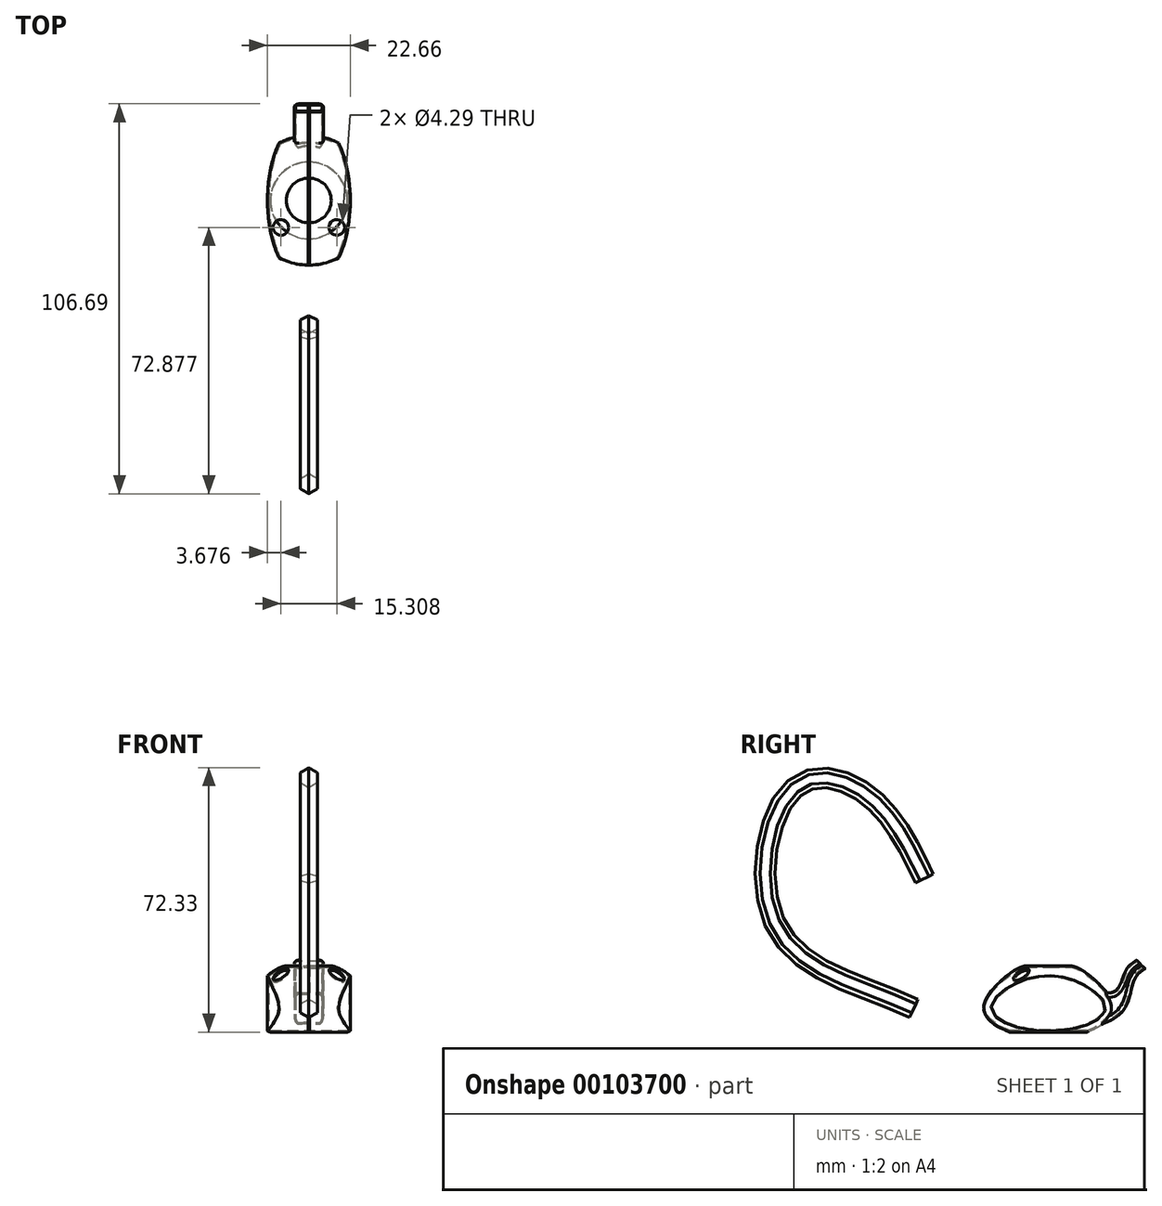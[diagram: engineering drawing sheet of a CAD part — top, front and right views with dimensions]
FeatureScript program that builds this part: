
annotation { "Feature Type Name" : "Feature", "Feature Type Description" : "" }
export const myFeature = defineFeature(function(context is Context, id is Id, definition is map)
    precondition{}
    {
        {
            assignVariable(context, id + "F0", {"name" : "shell_thickness", "anyValue" : 0.4});
        }
        {
            var Q0;
            Q0=qCreatedBy(makeId("Front.planeOp"),FACE);
            var sketch = newSketch(context, id + "F1", { "sketchPlane" : qUnion([Q0])});
            skLineSegment(sketch, "E0", {"start": v(0, 0) * mm, "end": v(-10.55, 0) * mm});
            skLineSegment(sketch, "E1", {"start": v(0, 0) * mm, "end": v(0, 20.96) * mm});
            skFitSpline(sketch, "E2", {"points": [v(-10.55, 0) * mm, v(-17.73, 6.7) * mm, v(-10.87, 15.78) * mm, v(-6.12, 18.17) * mm], "startDerivative": vector(-32.13, 11.4) * mm, "endDerivative": vector(19.24, 3.91) * mm});
            skLineSegment(sketch, "E3", {"start": v(-6.12, 18.17) * mm, "end": v(0, 18.17) * mm});
            skSolve(sketch);
        }
        {
            var Q0;
            Q0=makeQuery(id+"F1.imprint","IMPRINT",FACE,{"disambiguationData":[TD([[makeQuery(id+"F1.imprint","IMPRINT",EDGE,{"derivedFrom":sQuery(id+"F1.wireOp",EDGE,"E0")}),-1.0]])]});
            var Q1;
            Q1=sQuery(id+"F1.wireOp",EDGE,"E1");
            revolve(context, id + "F2", {"entities" : qUnion([Q0]), "axis" : qUnion([Q1]), "revolveType" : RevolveType.FULL});
        }
        {
            var Q0;
            Q0=qCreatedBy(makeId("Top.planeOp"),FACE);
            var sketch = newSketch(context, id + "F3", { "sketchPlane" : qUnion([Q0])});
            skEllipse(sketch, "E4", {"center": v(0, 0) * mm, "majorRadius": 22.7 * mm, "minorRadius": 11.33 * mm, "majorAxis": v(0, 1)});
            skSolve(sketch);
        }
        {
            var Q0;
            Q0=makeQuery(id+"F3.imprint","IMPRINT",FACE,{"disambiguationData":[TD([[makeQuery(id+"F3.imprint","IMPRINT",EDGE,{"derivedFrom":sQuery(id+"F3.wireOp",EDGE,"E4")}),1.0]])]});
            extrude(context, id + "F4", {"entities" : qUnion([Q0]), "operationType" : NewBodyOperationType.INTERSECT, "oppositeDirection" : true, "depth" : 25.4 * mm, "hasSecondDirection" : true, "secondDirectionOppositeDirection" : false, "secondDirectionDepth" : 25.4 * mm});
        }
        {
            var Q0;
            Q0=qCreatedBy(makeId("Right.planeOp"),FACE);
            var sketch = newSketch(context, id + "F5", { "sketchPlane" : qUnion([Q0])});
            skFitSpline(sketch, "E5", {"points": [v(13.8, 1.95) * mm, v(21.7, 8.15) * mm, v(23.96, 15.15) * mm, v(26.43, 17.37) * mm], "startDerivative": vector(35.23, 10.07) * mm, "endDerivative": vector(9.39, 6.72) * mm});
            skFitSpline(sketch, "E6", {"points": [v(14.11, 11.15) * mm, v(18.73, 11.69) * mm, v(21.6, 17.51) * mm, v(24.16, 19.7) * mm], "startDerivative": vector(18.22, -5.52) * mm, "endDerivative": vector(8.5, 6.7) * mm});
            skLineSegment(sketch, "E7", {"start": v(13.8, 1.95) * mm, "end": v(14.11, 11.15) * mm});
            skLineSegment(sketch, "E8", {"start": v(26.43, 17.37) * mm, "end": v(24.16, 19.7) * mm});
            skSolve(sketch);
        }
        {
            var Q0;
            Q0=makeQuery(id+"F5.imprint","IMPRINT",FACE,{"disambiguationData":[TD([[makeQuery(id+"F5.imprint","IMPRINT",EDGE,{"derivedFrom":sQuery(id+"F5.wireOp",EDGE,"E5")}),1.0]])]});
            extrude(context, id + "F6", {"entities" : qUnion([Q0]), "operationType" : NewBodyOperationType.ADD, "depth" : 4 * mm, "hasSecondDirection" : true, "secondDirectionOppositeDirection" : true, "secondDirectionDepth" : 4 * mm});
        }
        {
            var Q0;
            Q0=makeQuery(id+"F6.opExtrude","CAP_EDGE",EDGE,{"disambiguationData":[OSD([sQuery(id+"F5.wireOp",EDGE,"E6")])],"isStart":false});
            var Q1;
            Q1=makeQuery(id+"F6.opExtrude","CAP_EDGE",EDGE,{"disambiguationData":[OSD([sQuery(id+"F5.wireOp",EDGE,"E5")])],"isStart":false});
            var Q2;
            Q2=makeQuery(id+"F6.opExtrude","CAP_EDGE",EDGE,{"disambiguationData":[OSD([sQuery(id+"F5.wireOp",EDGE,"E6")])],"isStart":true});
            var Q3;
            Q3=makeQuery(id+"F6.opExtrude","CAP_EDGE",EDGE,{"disambiguationData":[OSD([sQuery(id+"F5.wireOp",EDGE,"E5")])],"isStart":true});
            fillet(context, id + "F7", {"entities" : qUnion([Q0, Q1, Q2, Q3]), "radius" : 1.27 * mm, "tangentPropagation" : true, "allowEdgeOverflow" : false});
        }
        {
            var Q0;
            Q0=makeQuery(id+"F2.opRevolve","SWEPT_BODY",BODY,{"disambiguationData":[OSD([sQuery(id+"F1.wireOp",EDGE,"E0"),sQuery(id+"F1.wireOp",EDGE,"E1"),sQuery(id+"F1.wireOp",EDGE,"E2"),sQuery(id+"F1.wireOp",EDGE,"E3")])]});
            transform(context, id + "F8", {"entities" : qUnion([Q0]), "transformType" : TransformType.TRANSLATION_3D, "dx" : 0 * mm, "dy" : 0 * mm, "dz" : 0 * mm, "makeCopy" : true});
        }
        {
            var Q0;
            Q0=qCreatedBy(makeId("Top.planeOp"),FACE);
            var sketch = newSketch(context, id + "F9", { "sketchPlane" : qUnion([Q0])});
            skLineSegment(sketch, "E9.bottom", {"start": v(-0.2, 30) * mm, "end": v(0.2, 30) * mm});
            skLineSegment(sketch, "E9.top", {"start": v(-0.2, -30) * mm, "end": v(0.2, -30) * mm});
            skLineSegment(sketch, "E9.left", {"start": v(-0.2, 30) * mm, "end": v(-0.2, -30) * mm});
            skLineSegment(sketch, "E9.right", {"start": v(0.2, 30) * mm, "end": v(0.2, -30) * mm});
            skPoint(sketch, "E9.middle", {"position": v(0, 0) * mm});
            skSolve(sketch);
        }
        {
            var Q0;
            Q0=makeQuery(id+"F9.imprint","IMPRINT",FACE,{"disambiguationData":[TD([[makeQuery(id+"F9.imprint","IMPRINT",EDGE,{"derivedFrom":sQuery(id+"F9.wireOp",EDGE,"E9.bottom")}),-1.0]])]});
            extrude(context, id + "F10", {"entities" : qUnion([Q0]), "endBound" : BoundingType.THROUGH_ALL, "depth" : 25 * mm});
        }
        {
            var Q0;
            Q0=makeQuery(id+"F8.opPattern","COPY",BODY,{"derivedFrom":makeQuery(id+"F2.opRevolve","SWEPT_BODY",BODY,{"disambiguationData":[OSD([sQuery(id+"F1.wireOp",EDGE,"E0"),sQuery(id+"F1.wireOp",EDGE,"E1"),sQuery(id+"F1.wireOp",EDGE,"E2"),sQuery(id+"F1.wireOp",EDGE,"E3")])]}),"instanceName":"1"});
            var Q1;
            Q1=makeQuery(id+"F10.opExtrude","SWEPT_BODY",BODY,{"disambiguationData":[OSD([sQuery(id+"F9.wireOp",EDGE,"E9.bottom"),sQuery(id+"F9.wireOp",EDGE,"E9.top"),sQuery(id+"F9.wireOp",EDGE,"E9.left"),sQuery(id+"F9.wireOp",EDGE,"E9.right")])]});
            booleanBodies(context, id + "F11", {"operationType" : BooleanOperationType.INTERSECTION, "tools" : qUnion([Q0, Q1])});
        }
        {
            var Q0;
            Q0=makeQuery(id+"F6.opExtrude","SWEPT_FACE",FACE,{"disambiguationData":[OSD([sQuery(id+"F5.wireOp",EDGE,"E8")])]});
            var Q1;
            Q1=makeQuery(id+"F2.opRevolve","SWEPT_BODY",BODY,{"disambiguationData":[OSD([sQuery(id+"F1.wireOp",EDGE,"E0"),sQuery(id+"F1.wireOp",EDGE,"E1"),sQuery(id+"F1.wireOp",EDGE,"E2"),sQuery(id+"F1.wireOp",EDGE,"E3")])]});
            shell(context, id + "F12", {"entities" : qUnion([Q0]), "parts" : qUnion([Q1]), "thickness" : (getVariable(context, 'shell_thickness')) * mm});
        }
        {
            var Q0;
            Q0=qCreatedBy(makeId("Right.planeOp"),FACE);
            var sketch = newSketch(context, id + "F13", { "sketchPlane" : qUnion([Q0])});
            skFitSpline(sketch, "E10", {"points": [v(-12.14, 2.5) * mm, v(-24.52, 9.88) * mm, v(-22.76, 22.14) * mm, v(-16.3, 20.98) * mm, v(-11.63, 13.86) * mm], "startDerivative": vector(-48.77, 22.4) * mm, "endDerivative": vector(16.06, -32.07) * mm});
            skSolve(sketch);
        }
        {
            var Q0;
            Q0=sQuery(id+"F13.wireOp",EDGE,"E10");
            var Q1;
            Q1=sQuery(id+"F13.wireOp",VERTEX,"E10.4.internal");
            cPlane(context, id + "F14", {"entities" : qUnion([Q0, Q1]), "cplaneType" : CPlaneType.CURVE_POINT, "offset" : 150 * mm, "width" : 150 * mm, "height" : 150 * mm});
        }
        {
            var Q0;
            Q0=qCreatedBy(id+"F14.planeOp",FACE);
            var sketch = newSketch(context, id + "F15", { "sketchPlane" : qUnion([Q0])});
            skCircle(sketch, "E11.cCircle", {"center": v(0, 3.84) * mm, "radius": 0.78 * mm, "construction": true});
            skLineSegment(sketch, "E11.0", {"start": v(-0.78, 3.39) * mm, "end": v(-0.78, 4.3) * mm});
            skLineSegment(sketch, "E11.1", {"start": v(-0.78, 4.3) * mm, "end": v(0, 4.74) * mm});
            skLineSegment(sketch, "E11.2", {"start": v(0, 4.74) * mm, "end": v(0.78, 4.3) * mm});
            skLineSegment(sketch, "E11.3", {"start": v(0.78, 4.3) * mm, "end": v(0.78, 3.39) * mm});
            skLineSegment(sketch, "E11.4", {"start": v(0.78, 3.39) * mm, "end": v(0, 2.93) * mm});
            skLineSegment(sketch, "E11.5", {"start": v(0, 2.93) * mm, "end": v(-0.78, 3.39) * mm});
            skPoint(sketch, "E11.0.midPoint", {"position": v(-0.78, 3.84) * mm});
            skSolve(sketch);
        }
        {
            var Q0;
            Q0=makeQuery(id+"F15.imprint","IMPRINT",FACE,{"disambiguationData":[TD([[makeQuery(id+"F15.imprint","IMPRINT",EDGE,{"derivedFrom":sQuery(id+"F15.wireOp",EDGE,"E11.0")}),-1.0]])]});
            var Q1;
            Q1=sQuery(id+"F13.wireOp",EDGE,"E10");
            sweep(context, id + "F16", {"profiles" : qUnion([Q0]), "path" : qUnion([Q1])});
        }
        {
            var Q0;
            Q0=makeQuery(id+"F2.opRevolve","SWEPT_FACE",FACE,{"disambiguationData":[OSD([sQuery(id+"F1.wireOp",EDGE,"E3")])]});
            var sketch = newSketch(context, id + "F17", { "sketchPlane" : qUnion([Q0])});
            skCircle(sketch, "E12", {"center": v(-7.65, -7.38) * mm, "radius": 2.15 * mm});
            skCircle(sketch, "E13.MirrorC", {"center": v(7.65, -7.38) * mm, "radius": 2.15 * mm});
            skSolve(sketch);
        }
        {
            var Q0;
            Q0 = qSketchRegion(id + "F17", true);
            var Q1;
            Q1=makeQuery(id+"F2.opRevolve","SWEPT_FACE",FACE,{"disambiguationData":[OSD([sQuery(id+"F1.wireOp",EDGE,"E2")])]});
            extrude(context, id + "F18", {"entities" : qUnion([Q0]), "operationType" : NewBodyOperationType.REMOVE, "oppositeDirection" : true, "endBoundEntityFace" : qUnion([Q1]), "depth" : 8.64 * mm});
        }
        {
            var Q0;
            Q0=makeQuery(id+"F16.opSweep","SWEPT_BODY",BODY,{"disambiguationData":[OSD([sQuery(id+"F13.wireOp",EDGE,"E10"),sQuery(id+"F15.wireOp",EDGE,"E11.0"),sQuery(id+"F15.wireOp",EDGE,"E11.1"),sQuery(id+"F15.wireOp",EDGE,"E11.2"),sQuery(id+"F15.wireOp",EDGE,"E11.3"),sQuery(id+"F15.wireOp",EDGE,"E11.4"),sQuery(id+"F15.wireOp",EDGE,"E11.5")])]});
            var Q1;
            Q1=qCreatedBy(makeId("Origin.pointOp"),VERTEX);
            transform(context, id + "F19", {"entities" : qUnion([Q0]), "transformType" : TransformType.SCALE_UNIFORMLY, "scale" : 3, "scalePoint" : qUnion([Q1]), "makeCopy" : false});
        }
    });
